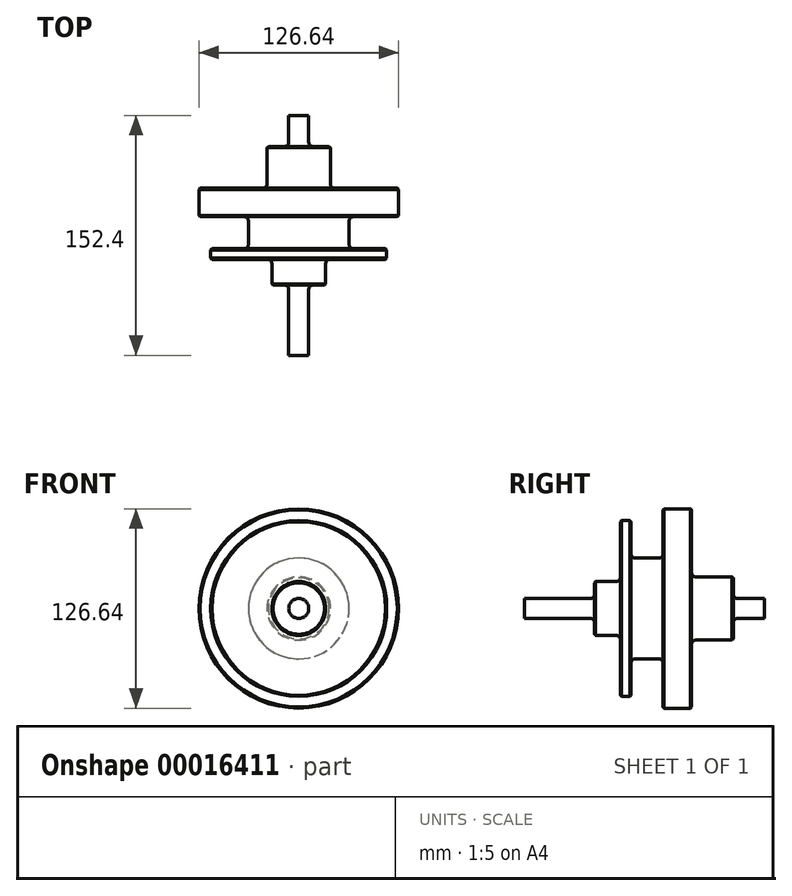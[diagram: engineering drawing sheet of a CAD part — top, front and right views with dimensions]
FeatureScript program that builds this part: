
annotation { "Feature Type Name" : "Feature", "Feature Type Description" : "" }
export const myFeature = defineFeature(function(context is Context, id is Id, definition is map)
    precondition{}
    {
        {
            var Q0;
            Q0=qCreatedBy(makeId("Front.planeOp"),FACE);
            var sketch = newSketch(context, id + "F0", { "sketchPlane" : qUnion([Q0])});
            skCircle(sketch, "E0", {"center": v(0, 0) * mm, "radius": 6.35 * mm});
            skSolve(sketch);
        }
        {
            var Q0;
            Q0=makeQuery(id+"F0.imprint","IMPRINT",FACE,{"disambiguationData":[TD([[makeQuery(id+"F0.imprint","IMPRINT",EDGE,{"derivedFrom":sQuery(id+"F0.wireOp",EDGE,"E0")}),1.0]])]});
            extrude(context, id + "F1", {"entities" : qUnion([Q0]), "oppositeDirection" : true, "depth" : 152.4 * mm});
        }
        {
            var Q0;
            Q0=qCreatedBy(makeId("Right.planeOp"),FACE);
            var sketch = newSketch(context, id + "F2", { "sketchPlane" : qUnion([Q0])});
            skLineSegment(sketch, "E1", {"start": v(-35.36, 0) * mm, "end": v(257.86, 0) * mm, "construction": true});
            skLineSegment(sketch, "E2", {"start": v(44.5, 0) * mm, "end": v(44.5, 17.13) * mm});
            skLineSegment(sketch, "E3", {"start": v(44.5, 17.13) * mm, "end": v(60.89, 17.13) * mm});
            skLineSegment(sketch, "E4", {"start": v(60.89, 17.13) * mm, "end": v(60.89, 55.87) * mm});
            skLineSegment(sketch, "E5", {"start": v(60.89, 55.87) * mm, "end": v(67.74, 55.87) * mm});
            skLineSegment(sketch, "E6", {"start": v(67.74, 55.87) * mm, "end": v(67.74, 32.02) * mm});
            skLineSegment(sketch, "E7", {"start": v(88, 32.02) * mm, "end": v(88, 63.32) * mm});
            skLineSegment(sketch, "E8", {"start": v(88, 63.32) * mm, "end": v(106.18, 63.32) * mm});
            skLineSegment(sketch, "E9", {"start": v(106.18, 63.32) * mm, "end": v(106.18, 20.11) * mm});
            skLineSegment(sketch, "E10", {"start": v(106.18, 20.11) * mm, "end": v(132.7, 20.11) * mm});
            skLineSegment(sketch, "E11", {"start": v(132.7, 20.11) * mm, "end": v(132.7, 0) * mm});
            skLineSegment(sketch, "E12", {"start": v(44.5, 0) * mm, "end": v(132.7, 0) * mm});
            skLineSegment(sketch, "E13", {"start": v(67.74, 32.02) * mm, "end": v(88, 32.02) * mm});
            skSolve(sketch);
        }
        {
            var Q0;
            Q0=makeQuery(id+"F2.imprint","IMPRINT",FACE,{"disambiguationData":[TD([[makeQuery(id+"F2.imprint","IMPRINT",EDGE,{"derivedFrom":sQuery(id+"F2.wireOp",EDGE,"E2")}),-1.0]])]});
            var Q1;
            Q1=sQuery(id+"F2.wireOp",EDGE,"E1");
            revolve(context, id + "F3", {"operationType" : NewBodyOperationType.ADD, "entities" : qUnion([Q0]), "axis" : qUnion([Q1]), "revolveType" : RevolveType.FULL});
        }
        {
            var Q0;
            Q0=makeQuery(id+"F3.opRevolve","SWEPT_EDGE",EDGE,{"disambiguationData":[OSD([sQuery(id+"F2.wireOp",EDGE,"E4"),sQuery(id+"F2.wireOp",EDGE,"E5")])]});
            var Q1;
            Q1=makeQuery(id+"F3.opRevolve","SWEPT_EDGE",EDGE,{"disambiguationData":[OSD([sQuery(id+"F2.wireOp",EDGE,"E5"),sQuery(id+"F2.wireOp",EDGE,"E6")])]});
            var Q2;
            Q2=makeQuery(id+"F3.opRevolve","SWEPT_EDGE",EDGE,{"disambiguationData":[OSD([sQuery(id+"F2.wireOp",EDGE,"E2"),sQuery(id+"F2.wireOp",EDGE,"E3")])]});
            var Q3;
            Q3=makeQuery(id+"F3.opRevolve","SWEPT_EDGE",EDGE,{"disambiguationData":[OSD([sQuery(id+"F2.wireOp",EDGE,"E7"),sQuery(id+"F2.wireOp",EDGE,"E8")])]});
            var Q4;
            Q4=makeQuery(id+"F3.opRevolve","SWEPT_EDGE",EDGE,{"disambiguationData":[OSD([sQuery(id+"F2.wireOp",EDGE,"E8"),sQuery(id+"F2.wireOp",EDGE,"E9")])]});
            var Q5;
            Q5=makeQuery(id+"F3.opRevolve","SWEPT_EDGE",EDGE,{"disambiguationData":[OSD([sQuery(id+"F2.wireOp",EDGE,"E10"),sQuery(id+"F2.wireOp",EDGE,"E11")])]});
            chamfer(context, id + "F4", {"entities" : qUnion([Q0, Q1, Q2, Q3, Q4, Q5]), "width" : 0.76 * mm, "tangentPropagation" : true});
        }
        {
            var Q0;
            Q0=makeQuery(id+"F3.opRevolve","SWEPT_EDGE",EDGE,{"disambiguationData":[OSD([sQuery(id+"F2.wireOp",EDGE,"e74f5cad-e23d-49e7-8f69-f76e36261e5e"),sQuery(id+"F2.wireOp",EDGE,"E7")])]});
            var Q1;
            Q1=makeQuery(id+"F3.opRevolve","SWEPT_EDGE",EDGE,{"disambiguationData":[OSD([sQuery(id+"F2.wireOp",EDGE,"E3"),sQuery(id+"F2.wireOp",EDGE,"E4")])]});
            var Q2;
            Q2=makeQuery(id+"F3.boolean.opBoolean","INTERSECT",EDGE,{"derivedFrom":[makeQuery(id+"F1.opExtrude","SWEPT_FACE",FACE,{"disambiguationData":[OSD([sQuery(id+"F0.wireOp",EDGE,"E0")])]}),makeQuery(id+"F3.opRevolve","SWEPT_FACE",FACE,{"disambiguationData":[OSD([sQuery(id+"F2.wireOp",EDGE,"E2")])]})]});
            var Q3;
            Q3=makeQuery(id+"F3.opRevolve","SWEPT_EDGE",EDGE,{"disambiguationData":[OSD([sQuery(id+"F2.wireOp",EDGE,"E6"),sQuery(id+"F2.wireOp",EDGE,"e74f5cad-e23d-49e7-8f69-f76e36261e5e")])]});
            var Q4;
            Q4=makeQuery(id+"F3.opRevolve","SWEPT_EDGE",EDGE,{"disambiguationData":[OSD([sQuery(id+"F2.wireOp",EDGE,"E9"),sQuery(id+"F2.wireOp",EDGE,"E10")])]});
            var Q5;
            Q5=makeQuery(id+"F3.boolean.opBoolean","INTERSECT",EDGE,{"derivedFrom":[makeQuery(id+"F1.opExtrude","SWEPT_FACE",FACE,{"disambiguationData":[OSD([sQuery(id+"F0.wireOp",EDGE,"E0")])]}),makeQuery(id+"F3.opRevolve","SWEPT_FACE",FACE,{"disambiguationData":[OSD([sQuery(id+"F2.wireOp",EDGE,"E11")])]})]});
            fillet(context, id + "F5", {"entities" : qUnion([Q0, Q1, Q2, Q3, Q4, Q5]), "radius" : 2.54 * mm, "tangentPropagation" : true, "rho" : 0, "crossSection" : FilletCrossSection.CONIC, "allowEdgeOverflow" : false});
        }
    });
